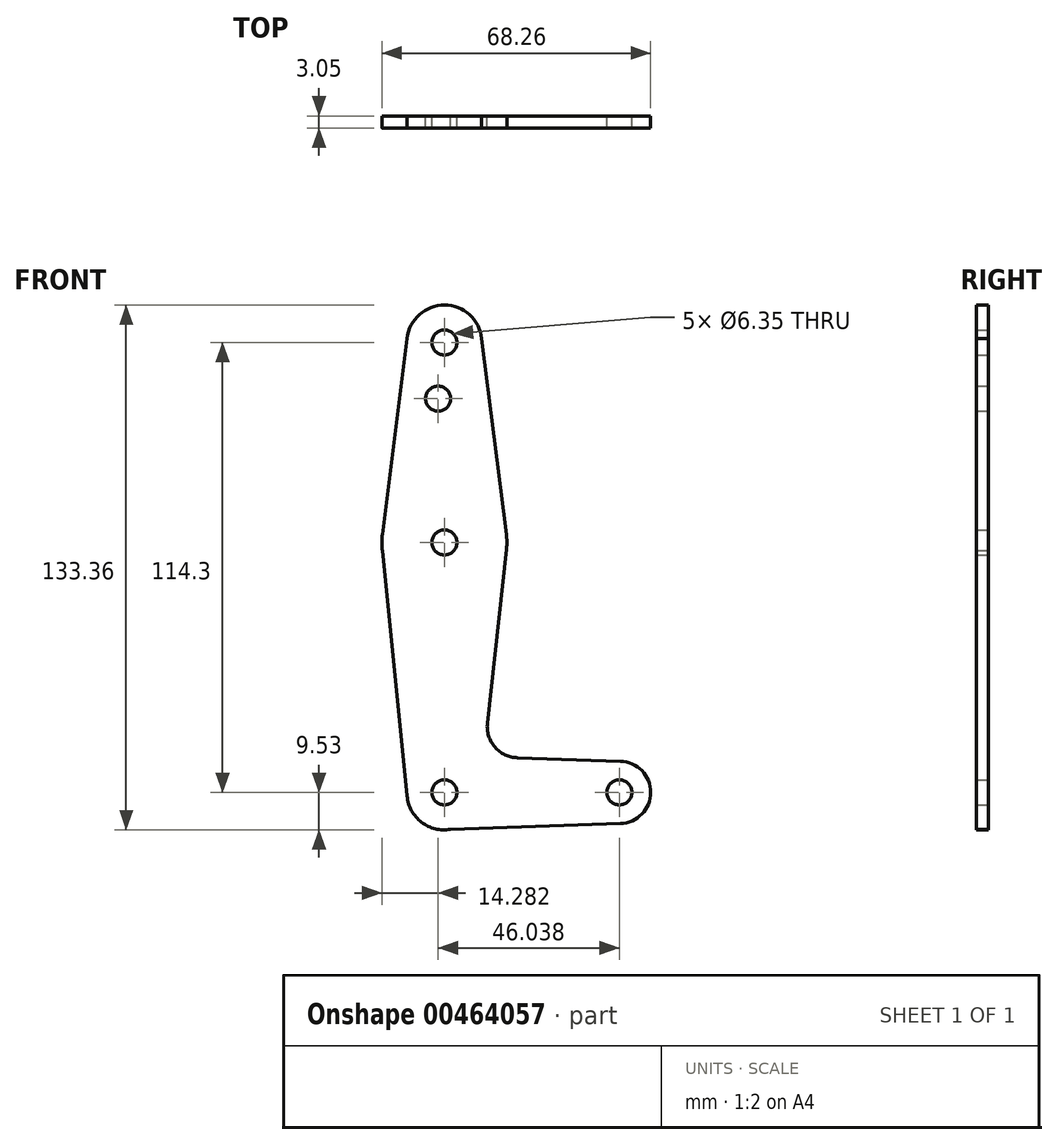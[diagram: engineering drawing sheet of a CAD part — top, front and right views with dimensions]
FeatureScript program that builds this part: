
annotation { "Feature Type Name" : "Feature", "Feature Type Description" : "" }
export const myFeature = defineFeature(function(context is Context, id is Id, definition is map)
    precondition{}
    {
        {
            var Q0;
            Q0=qCreatedBy(makeId("Front.planeOp"),FACE);
            var sketch = newSketch(context, id + "F0", { "sketchPlane" : qUnion([Q0])});
            skLineSegment(sketch, "E0", {"start": v(0, 0) * mm, "end": v(0, 114.3) * mm, "construction": true});
            skLineSegment(sketch, "E1", {"start": v(0, 0) * mm, "end": v(44.45, 0) * mm, "construction": true});
            skCircle(sketch, "E2", {"center": v(0, 0) * mm, "radius": 9.53 * mm});
            skCircle(sketch, "E3", {"center": v(0, 114.3) * mm, "radius": 9.53 * mm});
            skCircle(sketch, "E4", {"center": v(0, 63.5) * mm, "radius": 15.88 * mm});
            skCircle(sketch, "E5", {"center": v(44.45, 0) * mm, "radius": 7.94 * mm});
            skLineSegment(sketch, "E6", {"start": v(-9.43, 115.63) * mm, "end": v(-15.75, 65.48) * mm});
            skLineSegment(sketch, "E7", {"start": v(9.42, 115.72) * mm, "end": v(15.75, 65.49) * mm});
            skLineSegment(sketch, "E8", {"start": v(-15.75, 61.52) * mm, "end": v(-9.48, -0.95) * mm});
            skLineSegment(sketch, "E9", {"start": v(15.78, 61.77) * mm, "end": v(10.93, 17.61) * mm});
            skLineSegment(sketch, "E10", {"start": v(18.57, 8.8) * mm, "end": v(44.71, 7.93) * mm});
            skLineSegment(sketch, "E11", {"start": v(1.57, -9.4) * mm, "end": v(44.72, -7.93) * mm});
            skCircle(sketch, "E12", {"center": v(0, 114.3) * mm, "radius": 3.18 * mm});
            skCircle(sketch, "E13", {"center": v(-1.59, 100.03) * mm, "radius": 3.18 * mm});
            skArc(sketch, "E14.filletArc", {"start": v(10.93, 17.61) * mm, "mid": v(12.83, 11.54) * mm, "end": v(18.57, 8.8) * mm});
            skCircle(sketch, "E15", {"center": v(0, 0) * mm, "radius": 3.18 * mm});
            skCircle(sketch, "E16", {"center": v(44.45, 0) * mm, "radius": 3.18 * mm});
            skCircle(sketch, "E17", {"center": v(0, 63.5) * mm, "radius": 3.18 * mm});
            skSolve(sketch);
        }
        {
            var Q0;
            Q0 = qSketchRegion(id + "F0", true);
            extrude(context, id + "F1", {"entities" : qUnion([Q0]), "depth" : 3.05 * mm});
        }
    });
